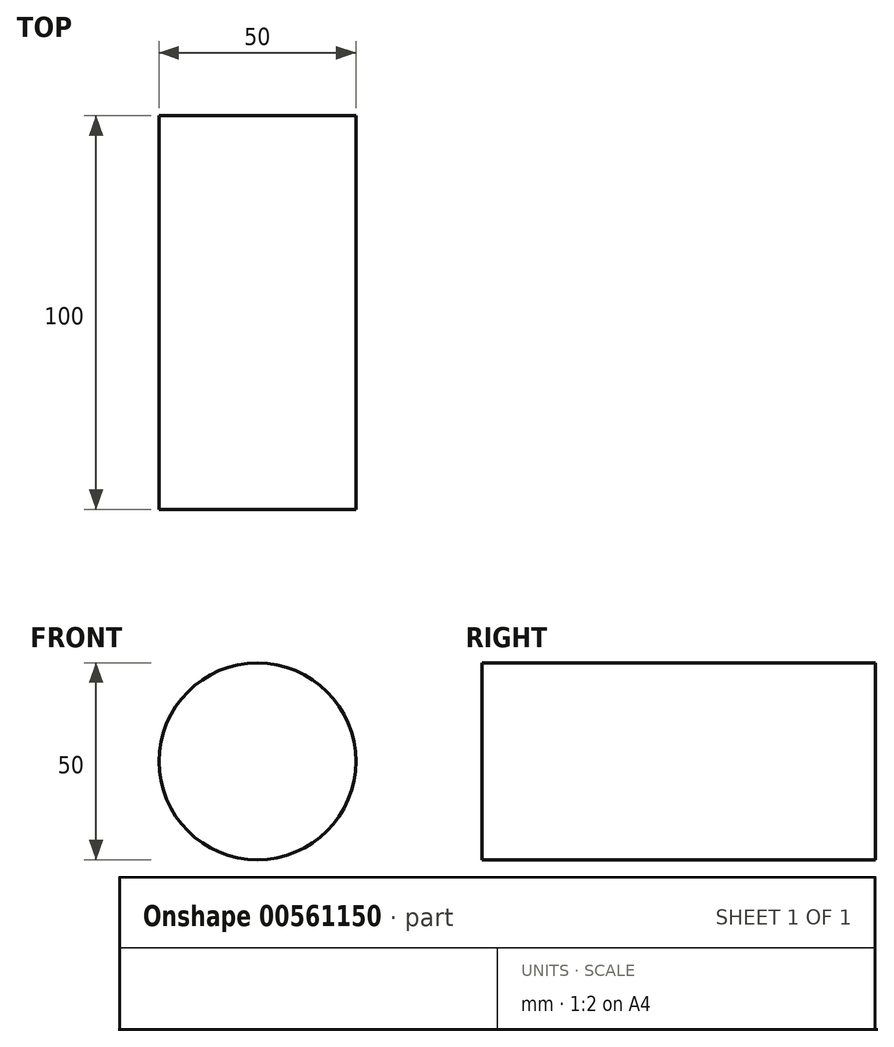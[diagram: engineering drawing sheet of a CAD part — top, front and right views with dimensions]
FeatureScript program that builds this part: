
annotation { "Feature Type Name" : "Feature", "Feature Type Description" : "" }
export const myFeature = defineFeature(function(context is Context, id is Id, definition is map)
    precondition{}
    {
        {
            var Q0;
            Q0=qCreatedBy(makeId("Front.planeOp"),FACE);
            var sketch = newSketch(context, id + "F0", { "sketchPlane" : qUnion([Q0])});
            skCircle(sketch, "E0", {"center": v(0, 0) * mm, "radius": 25 * mm});
            skSolve(sketch);
        }
        {
            var Q0;
            Q0 = qSketchRegion(id + "F0", true);
            extrude(context, id + "F1", {"entities" : qUnion([Q0]), "depth" : 100 * mm, "offsetDistance" : 25 * mm});
        }
        {
            var Q0;
            Q0=qCreatedBy(makeId("Front.planeOp"),FACE);
            var sketch = newSketch(context, id + "F2", { "sketchPlane" : qUnion([Q0])});
            skCircle(sketch, "E1", {"center": v(0, 0) * mm, "radius": 15 * mm});
            skSolve(sketch);
        }
        {
            var Q0;
            Q0 = qSketchRegion(id + "F2", true);
            var Q1;
            Q1=sQuery(id+"F2.wireOp",EDGE,"E1");
            extrude(context, id + "F3", {"entities" : qUnion([Q0]), "bodyType" : ToolBodyType.SURFACE, "operationType" : NewBodyOperationType.INTERSECT, "surfaceEntities" : qUnion([Q1]), "depth" : 100 * mm, "offsetDistance" : 25 * mm});
        }
    });
